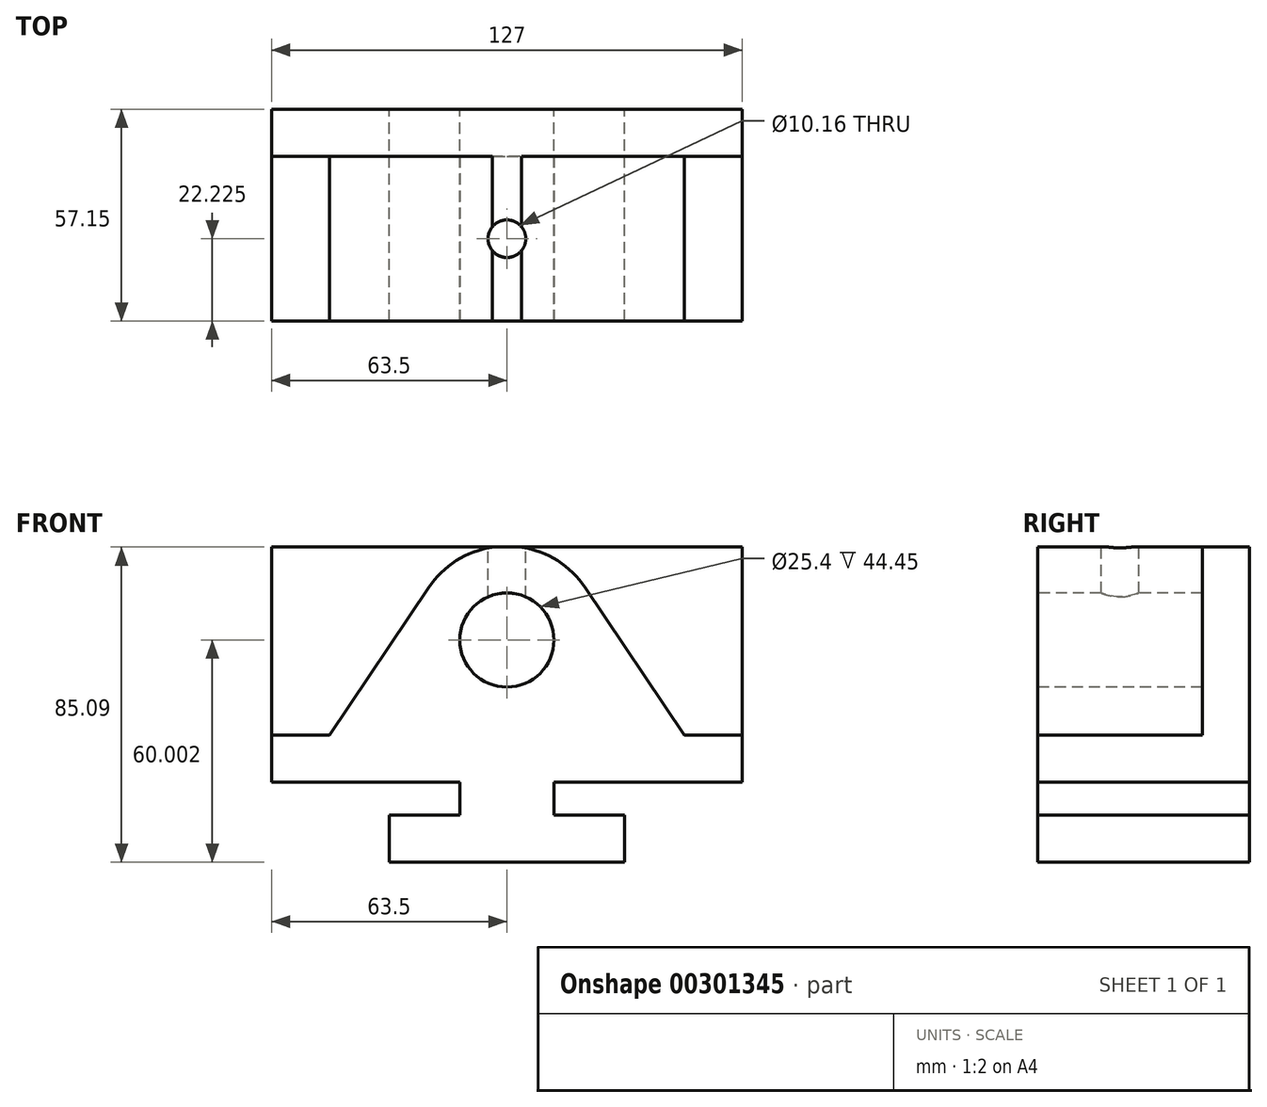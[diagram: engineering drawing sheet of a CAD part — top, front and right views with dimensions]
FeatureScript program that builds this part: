
annotation { "Feature Type Name" : "Feature", "Feature Type Description" : "" }
export const myFeature = defineFeature(function(context is Context, id is Id, definition is map)
    precondition{}
    {
        {
            var Q0;
            Q0=qCreatedBy(makeId("Front.planeOp"),FACE);
            var sketch = newSketch(context, id + "F0", { "sketchPlane" : qUnion([Q0])});
            skLineSegment(sketch, "E0", {"start": v(0, 0) * mm, "end": v(63.5, 0) * mm});
            skLineSegment(sketch, "E1", {"start": v(63.5, 0) * mm, "end": v(63.5, 12.7) * mm});
            skLineSegment(sketch, "E2", {"start": v(63.5, 12.7) * mm, "end": v(44.45, 12.7) * mm});
            skLineSegment(sketch, "E3", {"start": v(44.45, 12.7) * mm, "end": v(44.45, 21.59) * mm});
            skLineSegment(sketch, "E4", {"start": v(44.45, 21.59) * mm, "end": v(95.25, 21.59) * mm});
            skLineSegment(sketch, "E5", {"start": v(0, 0) * mm, "end": v(0, 12.7) * mm});
            skLineSegment(sketch, "E6", {"start": v(0, 12.7) * mm, "end": v(19.05, 12.7) * mm});
            skLineSegment(sketch, "E7", {"start": v(19.05, 12.7) * mm, "end": v(19.05, 21.6) * mm});
            skLineSegment(sketch, "E8", {"start": v(19.05, 21.59) * mm, "end": v(-31.75, 21.59) * mm});
            skLineSegment(sketch, "E9", {"start": v(-31.75, 21.59) * mm, "end": v(-31.75, 34.3) * mm});
            skLineSegment(sketch, "E10", {"start": v(-31.75, 34.3) * mm, "end": v(-15.88, 34.3) * mm});
            skLineSegment(sketch, "E11", {"start": v(95.25, 21.59) * mm, "end": v(95.25, 34.3) * mm});
            skLineSegment(sketch, "E12", {"start": v(95.25, 34.3) * mm, "end": v(79.38, 34.3) * mm});
            skLineSegment(sketch, "E13", {"start": v(-15.88, 34.3) * mm, "end": v(10.66, 73.84) * mm});
            skLineSegment(sketch, "E14", {"start": v(79.38, 34.3) * mm, "end": v(52.84, 73.84) * mm});
            skArc(sketch, "E15", {"start": v(10.66, 73.84) * mm, "mid": v(31.75, 85.1) * mm, "end": v(52.84, 73.84) * mm});
            skLineSegment(sketch, "E16", {"start": v(-31.75, 34.3) * mm, "end": v(-31.75, 85.1) * mm});
            skPoint(sketch, "E16.endSnap0", {"position": v(31.75, 85.1) * mm});
            skLineSegment(sketch, "E17", {"start": v(-31.75, 85.1) * mm, "end": v(95.25, 85.1) * mm});
            skLineSegment(sketch, "E18", {"start": v(95.25, 85.1) * mm, "end": v(95.25, 34.3) * mm});
            skSolve(sketch);
        }
        {
            var Q0;
            Q0 = qSketchRegion(id + "F0", true);
            extrude(context, id + "F1", {"entities" : qUnion([Q0]), "depth" : 57.15 * mm});
        }
        {
            var Q0;
            Q0=makeQuery(id+"F1.opExtrude","CAP_FACE",FACE,{"disambiguationData":[OSD([sQuery(id+"F0.wireOp",EDGE,"E0"),sQuery(id+"F0.wireOp",EDGE,"E1"),sQuery(id+"F0.wireOp",EDGE,"E2"),sQuery(id+"F0.wireOp",EDGE,"E3"),sQuery(id+"F0.wireOp",EDGE,"E4"),sQuery(id+"F0.wireOp",EDGE,"E5"),sQuery(id+"F0.wireOp",EDGE,"E6"),sQuery(id+"F0.wireOp",EDGE,"E7"),sQuery(id+"F0.wireOp",EDGE,"E8"),sQuery(id+"F0.wireOp",EDGE,"E9"),sQuery(id+"F0.wireOp",EDGE,"E11"),sQuery(id+"F0.wireOp",EDGE,"E16"),sQuery(id+"F0.wireOp",EDGE,"E17"),sQuery(id+"F0.wireOp",EDGE,"E18")])],"isStart":false});
            var sketch = newSketch(context, id + "F2", { "sketchPlane" : qUnion([Q0])});
            skLineSegment(sketch, "E19", {"start": v(-31.75, 34.3) * mm, "end": v(-16.12, 34.3) * mm});
            skLineSegment(sketch, "E20", {"start": v(-16.12, 34.29) * mm, "end": v(10.66, 74.16) * mm});
            skLineSegment(sketch, "E21", {"start": v(95.25, 34.3) * mm, "end": v(79.62, 34.3) * mm});
            skLineSegment(sketch, "E22", {"start": v(79.62, 34.3) * mm, "end": v(52.84, 74.16) * mm});
            skArc(sketch, "E23", {"start": v(10.66, 74.16) * mm, "mid": v(31.75, 85.4) * mm, "end": v(52.84, 74.16) * mm});
            skLineSegment(sketch, "E24", {"start": v(-31.75, 34.3) * mm, "end": v(-31.75, 85.1) * mm});
            skLineSegment(sketch, "E25", {"start": v(-31.75, 85.1) * mm, "end": v(95.25, 85.1) * mm});
            skLineSegment(sketch, "E26", {"start": v(95.25, 85.1) * mm, "end": v(95.25, 34.3) * mm});
            skCircle(sketch, "E27", {"center": v(31.75, 60) * mm, "radius": 12.7 * mm});
            skSolve(sketch);
        }
        {
            var Q0;
            Q0 = qSketchRegion(id + "F2", true);
            extrude(context, id + "F3", {"entities" : qUnion([Q0]), "operationType" : NewBodyOperationType.REMOVE, "oppositeDirection" : true, "depth" : 44.45 * mm});
        }
        {
            var Q0;
            Q0=makeQuery(id+"F1.opExtrude","SWEPT_FACE",FACE,{"disambiguationData":[OSD([sQuery(id+"F0.wireOp",EDGE,"E17")])]});
            var sketch = newSketch(context, id + "F4", { "sketchPlane" : qUnion([Q0])});
            skCircle(sketch, "E28", {"center": v(31.75, -34.93) * mm, "radius": 5.08 * mm});
            skPoint(sketch, "E28.centerSnap0", {"position": v(35.72, -34.93) * mm});
            skSolve(sketch);
        }
        {
            var Q0;
            Q0 = qSketchRegion(id + "F4", true);
            extrude(context, id + "F5", {"entities" : qUnion([Q0]), "operationType" : NewBodyOperationType.REMOVE, "oppositeDirection" : true, "depth" : 25.4 * mm});
        }
    });
